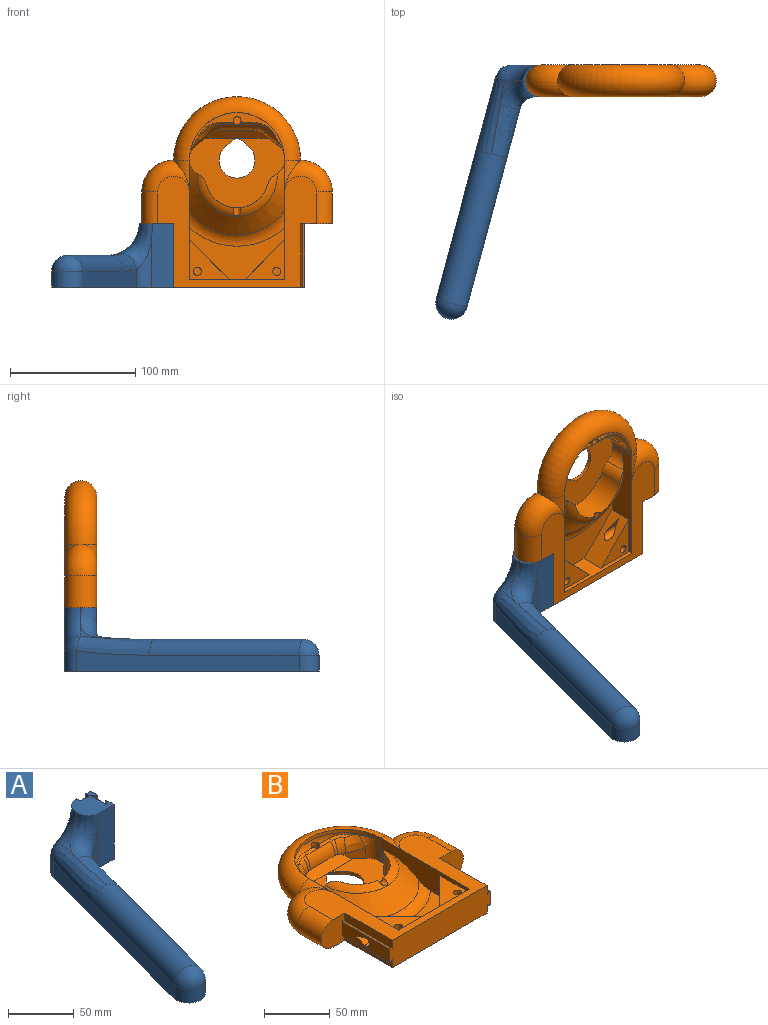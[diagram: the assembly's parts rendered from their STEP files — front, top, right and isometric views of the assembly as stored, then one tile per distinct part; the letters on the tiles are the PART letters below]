
ASSEMBLY  parts=2 mates=1
PART A: 35 faces, bbox 98.5x203.9x53 mm
  f0: plane 9.53x5.59mm, normal (0,1,0), area 53.2mm2, adj f24,f25,f26,f34
  f1: plane 50.8x37.41mm, normal (0,1,0), area 1193.4mm2, adj f2,f4,f9,f19,f20,f24,f25,f28
  f2: plane 28.01x25.75mm, normal (0,0,1), area 544.5mm2, adj f1,f3,f4,f7,f8,f17,f20,f24
  f3: cylinder r=25.4mm len=9.81mm, axis (0,-1,0), area 0.9mm2, adj f2,f17,f20
  f4: plane 50.8x7.69mm, normal (1,0,0), area 390.4mm2, adj f1,f2,f9,f29
  f5: plane 178.5x48.34mm, normal (-0.97,0.26,0), area 2404.3mm2, adj f9,f15,f18,f19,f23
  f6: plane 159.18x42.81mm, normal (0.97,-0.26,0), area 2110.6mm2, adj f9,f14,f15,f18,f21
  f7: plane 51.13x18.25mm, normal (0,-1,0), area 901.7mm2, adj f2,f8,f9,f14,f17
  f8: plane 50.8x7.69mm, normal (1,0,0), area 390.4mm2, adj f2,f7,f9,f30
  f9: plane 203.2x97.75mm, normal (0,0,-1), area 5844mm2, adj f1,f4,f5,f6,f7,f8,f10,f11
  f10: plane 50.04x2.13mm, normal (-0.71,-0.71,0), area 150.6mm2, adj f9,f11,f29,f33
  f11: plane 50.04x13.21mm, normal (1,0,0), area 660.9mm2, adj f9,f10,f12,f32
  f12: plane 50.04x2.13mm, normal (-0.71,0.71,0), area 150.6mm2, adj f9,f11,f30,f31
  f13: cylinder r=25.4mm len=18.83mm, axis (0,-1,0), area 179.5mm2, adj f17,f20,f23
  f14: cylinder r=12.7mm len=36.09mm, axis (0,0,1), area 418.1mm2, adj f6,f7,f9,f17
  f15: cylinder r=12.7mm len=24.97mm, axis (0,0,-1), area 506.7mm2, adj f5,f6,f9,f16
  f16: sphere r=12.7mm, area 506.7mm2, adj f15,f18
  f17: bspline ~38.25x29.94mm, area 798.1mm2, adj f2,f3,f7,f13,f14,f21
  f18: cylinder r=12.7mm len=125.95mm, axis (-0.26,-0.97,0), area 4930.9mm2, adj f5,f6,f16,f21,f23
  f19: cylinder r=12.7mm len=16.07mm, axis (0,0,-1), area 267.1mm2, adj f1,f5,f9,f22
  f20: torus R=38.1mm, axis (0,-1,0), area 687mm2, adj f1,f2,f3,f13,f22
  f21: bspline ~42.89x22.88mm, area 874.6mm2, adj f6,f17,f18,f23
  f22: sphere r=12.7mm, area 108.4mm2, adj f19,f20,f23
  f23: bspline ~61.71x22.7mm, area 1039.4mm2, adj f5,f13,f18,f21,f22
  f24: plane 15.33x6.35mm, normal (-1,0,0), area 69mm2, adj f0,f1,f2,f26,f27,f28,f34
  f25: plane 15.33x6.35mm, normal (1,0,0), area 69mm2, adj f0,f1,f2,f26,f27,f28,f34
  f26: plane 9.53x3.18mm, normal (0,0,-1), area 30.2mm2, adj f0,f24,f25,f27
  f27: plane 9.53x6.35mm, normal (0,1,0), area 60.5mm2, adj f24,f25,f26,f28
  f28: plane 9.53x6.35mm, normal (0,0.38,0.92), area 65.5mm2, adj f1,f24,f25,f27
  f29: cylinder r=0.76mm len=50.8mm, axis (0,0,1), area 90.8mm2, adj f2,f4,f9,f10,f33
  f30: cylinder r=0.76mm len=50.8mm, axis (0,0,1), area 90.8mm2, adj f2,f8,f9,f12,f31
  f31: cylinder r=0.76mm len=4.51mm, axis (-0.71,-0.71,0), area 5.2mm2, adj f2,f12,f30,f32
  f32: cylinder r=0.76mm len=16.89mm, axis (0,1,0), area 18mm2, adj f2,f11,f31,f33
  f33: cylinder r=0.76mm len=4.51mm, axis (0.71,-0.71,0), area 5.2mm2, adj f2,f10,f29,f32
  f34: cylinder r=0.76mm len=9.53mm, axis (-1,0,0), area 11.4mm2, adj f0,f2,f24,f25
PART B: 87 faces, bbox 170.6x170.6x47.6 mm
  f0: plane 76.2x55.57mm, normal (0,0,1), area 2861mm2, adj f3,f26,f29,f30,f34,f35,f36,f38
  f1: plane 31.75x31.75mm, normal (-0.71,0.71,0), area 758.2mm2, adj f9,f25,f28,f56,f57,f58,f60
  f2: plane 31.75x31.75mm, normal (0.71,0.71,0), area 758.2mm2, adj f9,f27,f28,f53,f54,f55,f59
  f3: cylinder r=25.4mm len=49.01mm, axis (0,0,-1), area 1436.4mm2, adj f0,f4,f33,f35,f37,f38,f40,f41
  f4: torus R=23.11mm, axis (0,0,1), area 650.9mm2, adj f3,f8,f31,f32,f40,f41,f52
  f5: plane 25.4x25.4mm, normal (0,-1,0), area 537mm2, adj f6,f10,f11,f12,f17,f47,f48,f49
  f6: plane 50.8x7.94mm, normal (-1,0,0), area 403.2mm2, adj f5,f11,f13,f49
  f7: plane 50.8x7.94mm, normal (1,0,0), area 403.2mm2, adj f10,f13,f15,f43
  f8: cylinder r=12.7mm len=18.01mm, axis (0,0,-1), area 180.9mm2, adj f4,f26,f31,f37,f40
  f9: plane 76.2x41.43mm, normal (0,0,1), area 1367mm2, adj f1,f2,f25,f27,f28,f39
  f10: plane 139.7x127mm, normal (0,0,-1), area 12393.6mm2, adj f5,f7,f12,f13,f15,f16,f17,f18
  f11: plane 127x88.9mm, normal (0,0,1), area 3571.2mm2, adj f5,f6,f13,f14,f15,f16,f17,f18
  f12: plane 50.8x7.94mm, normal (-1,0,0), area 403.2mm2, adj f5,f10,f13,f48
  f13: plane 107.95x25.4mm, normal (0,-1,0), area 2658.4mm2, adj f6,f7,f10,f11,f12,f14,f42,f43
  f14: plane 50.8x7.94mm, normal (1,0,0), area 403.2mm2, adj f11,f13,f15,f42
  f15: plane 25.4x25.4mm, normal (0,-1,0), area 537mm2, adj f7,f10,f11,f14,f16,f42,f43,f44
  f16: cylinder r=12.7mm len=25.4mm, axis (0,-1,0), area 1013.4mm2, adj f10,f11,f15,f19
  f17: cylinder r=12.7mm len=25.4mm, axis (0,1,0), area 1013.4mm2, adj f5,f10,f11,f18
  f18: torus R=12.7mm, axis (0,0,1), area 1884.7mm2, adj f10,f11,f17,f20,f22
  f19: torus R=12.7mm, axis (0,0,1), area 1884.7mm2, adj f10,f11,f16,f21,f24
  f20: cylinder r=12.7mm len=25.4mm, axis (0,-1,0), area 253.4mm2, adj f10,f18,f23
  f21: cylinder r=12.7mm len=25.4mm, axis (0,1,0), area 253.4mm2, adj f10,f19,f23
  f22: cylinder r=12.7mm len=25.4mm, axis (0,1,0), area 253.4mm2, adj f18,f23,f27
  f23: torus R=38.1mm, axis (0,0,1), area 5789mm2, adj f10,f20,f21,f22,f24,f26
  f24: cylinder r=12.7mm len=25.4mm, axis (0,-1,0), area 253.4mm2, adj f19,f23,f25
  f25: plane 109.27x36.25mm, normal (-1,0,0), area 1078.2mm2, adj f1,f9,f11,f24,f26,f28,f31,f39
  f26: cylinder r=38.1mm len=76.2mm, axis (0,0,1), area 466.6mm2, adj f0,f8,f23,f25,f27,f32,f34,f36
  f27: plane 109.27x36.25mm, normal (1,0,0), area 1078.2mm2, adj f2,f9,f11,f22,f26,f28,f31,f39
  f28: plane 76.2x22.23mm, normal (0,1,0), area 483.9mm2, adj f1,f2,f9,f11,f25,f27,f59,f60
  f29: sphere r=14.61mm, area 219.3mm2, adj f0,f10,f30
  f30: cone r=0mm half-angle=45deg, axis (0,-1,0), area 91.3mm2, adj f0,f10,f29,f73
  f31: cone r=50.8mm half-angle=45deg, axis (0,0,-1), area 2656.4mm2, adj f4,f8,f25,f27,f32,f39
  f32: cylinder r=12.7mm len=18.01mm, axis (0,0,-1), area 180.9mm2, adj f4,f26,f31,f33,f41
  f33: plane 25.4x16.1mm, normal (0,0,-1), area 201.6mm2, adj f3,f32,f34,f35,f41
  f34: plane 25.4x1.59mm, normal (-1,0,0), area 40.3mm2, adj f0,f26,f33,f35
  f35: plane 16.1x1.59mm, normal (0,1,0), area 25.6mm2, adj f0,f3,f33,f34
  f36: plane 25.4x1.59mm, normal (1,0,0), area 40.3mm2, adj f0,f26,f37,f38
  f37: plane 25.4x16.1mm, normal (0,0,-1), area 201.6mm2, adj f3,f8,f36,f38,f40
  f38: plane 16.1x1.59mm, normal (0,1,0), area 25.6mm2, adj f0,f3,f36,f37
  f39: torus R=56.06mm, axis (0,0,1), area 862.3mm2, adj f9,f25,f27,f31
  f40: cylinder r=12.7mm len=20.64mm, axis (0,0,-1), area 206.4mm2, adj f3,f4,f8,f37
  f41: cylinder r=12.7mm len=20.64mm, axis (0,0,-1), area 206.4mm2, adj f3,f4,f32,f33
  f42: plane 50.8x1.87mm, normal (-0.71,0,0.71), area 134.6mm2, adj f13,f14,f15,f46
  f43: plane 50.8x1.87mm, normal (-0.71,0,-0.71), area 134.6mm2, adj f7,f13,f15,f45
  f44: plane 50.8x12.2mm, normal (1,0,0), area 550.8mm2, adj f13,f15,f45,f46,f56,f57,f58
  f45: cylinder r=0.76mm len=50.8mm, axis (0,1,0), area 91.2mm2, adj f13,f15,f43,f44
  f46: cylinder r=0.76mm len=50.8mm, axis (0,1,0), area 91.2mm2, adj f13,f15,f42,f44
  f47: plane 50.8x12.2mm, normal (-1,0,0), area 550.8mm2, adj f5,f13,f50,f51,f53,f54,f55
  f48: plane 50.8x1.87mm, normal (0.71,0,-0.71), area 134.6mm2, adj f5,f12,f13,f51
  f49: plane 50.8x1.87mm, normal (0.71,0,0.71), area 134.6mm2, adj f5,f6,f13,f50
  f50: cylinder r=0.76mm len=50.8mm, axis (0,1,0), area 91.2mm2, adj f5,f13,f47,f49
  f51: cylinder r=0.76mm len=50.8mm, axis (0,1,0), area 91.2mm2, adj f5,f13,f47,f48
  f52: cylinder r=3.17mm len=6.54mm, axis (0,1,0), area 47.2mm2, adj f3,f4
  f53: plane 27.06x8.84mm, normal (0,-0.38,0.92), area 216.6mm2, adj f2,f47,f54,f55
  f54: cylinder r=3.96mm len=32.56mm, axis (-1,0,0), area 473.6mm2, adj f2,f47,f53,f55
  f55: plane 27.06x8.84mm, normal (0,-0.38,-0.92), area 216.6mm2, adj f2,f47,f53,f54
  f56: plane 27.06x8.84mm, normal (0,-0.38,-0.92), area 216.6mm2, adj f1,f44,f57,f58
  f57: cylinder r=3.96mm len=32.56mm, axis (-1,0,0), area 473.6mm2, adj f1,f44,f56,f58
  f58: plane 27.06x8.84mm, normal (0,-0.38,0.92), area 216.6mm2, adj f1,f44,f56,f57
  f59: plane 31.75x31.75mm, normal (0,0,1), area 472.4mm2, adj f2,f27,f28,f85
  f60: plane 31.75x31.75mm, normal (0,0,1), area 472.4mm2, adj f1,f25,f28,f83
  f61: plane 6.35x6.35mm, normal (0,0,1), area 31.7mm2, adj f62
  f62: cylinder r=3.17mm len=19.05mm, axis (0,0,-1), area 380mm2, adj f61,f63,f71
  f63: plane 76.2x35.47mm, normal (0,0,1), area 324.1mm2, adj f26,f62,f70,f71,f72,f74,f75,f81
  f64: plane 11.99x9.99mm, normal (-0.63,-0.78,0), area 104.2mm2, adj f0,f66,f68,f73,f81
  f65: plane 11.99x9.99mm, normal (0.63,-0.78,0), area 104.2mm2, adj f0,f67,f69,f73,f75
  f66: cylinder r=12.7mm len=5.56mm, axis (0,0,1), area 7.9mm2, adj f64,f73,f80
  f67: cylinder r=12.7mm len=5.56mm, axis (0,0,-1), area 7.9mm2, adj f65,f73,f76
  f68: cylinder r=12.7mm len=18.82mm, axis (0,0,1), area 152.9mm2, adj f0,f26,f64,f82
  f69: cylinder r=12.7mm len=18.82mm, axis (0,0,1), area 152.9mm2, adj f0,f26,f65,f74
  f70: cone r=19.05mm half-angle=45deg, axis (0,0,1), area 37mm2, adj f63,f71,f75,f76,f77
  f71: plane 29.92x4.88mm, normal (0,-0.71,0.71), area 55.6mm2, adj f62,f63,f70,f72,f78
  f72: cone r=19.05mm half-angle=45deg, axis (0,0,1), area 37.1mm2, adj f63,f71,f79,f80,f81
  f73: plane 52.2x7.03mm, normal (0,-0.71,0.71), area 385.3mm2, adj f0,f30,f64,f65,f66,f67,f77,f78
  f74: bspline ~21.09x18.27mm, area 68.2mm2, adj f26,f63,f69,f75
  f75: bspline ~15.59x14.44mm, area 167mm2, adj f63,f65,f70,f74,f76
  f76: torus R=28.57mm, axis (0,0,-1), area 86.7mm2, adj f67,f70,f75,f77
  f77: bspline ~11.54x6.03mm, area 33.3mm2, adj f70,f73,f76,f78
  f78: cylinder r=15.88mm len=26.74mm, axis (-1,0,0), area 327.4mm2, adj f71,f73,f77,f79
  f79: bspline ~11.84x8.72mm, area 33.3mm2, adj f72,f73,f78,f80
  f80: torus R=28.57mm, axis (0,0,-1), area 86.7mm2, adj f66,f72,f79,f81
  f81: bspline ~17.29x16.26mm, area 167mm2, adj f63,f64,f72,f80,f82
  f82: bspline ~21.09x18.27mm, area 68.2mm2, adj f26,f63,f68,f81
  f83: cylinder r=3.17mm len=19.05mm, axis (0,0,1), area 380mm2, adj f60,f84
  f84: plane 6.35x6.35mm, normal (0,0,1), area 31.7mm2, adj f83
  f85: cylinder r=3.17mm len=19.05mm, axis (0,0,1), area 380mm2, adj f59,f86
  f86: plane 6.35x6.35mm, normal (0,0,1), area 31.7mm2, adj f85
PLACE A t=(-50.55,-25.4,0.18)mm
PLACE B rot(axis=(1,0,0),90deg) t=(0,0,76.2)mm
MATE planar B.f47 <-> A.f11  axis (-1,0,0) through (-53.98,-12.7,25.2)mm
